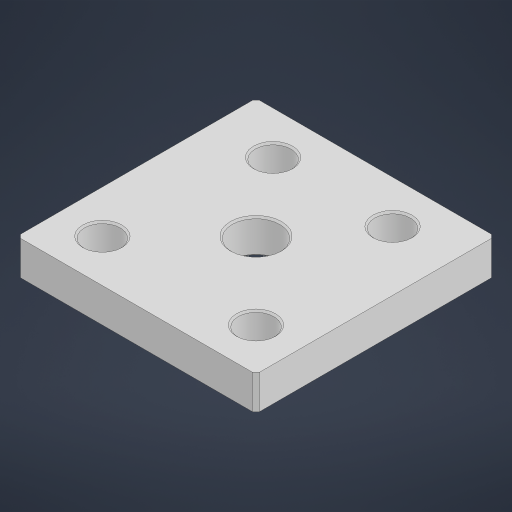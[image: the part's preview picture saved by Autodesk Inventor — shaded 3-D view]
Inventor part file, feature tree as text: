
AUTODESK INVENTOR PART (.ipt)
format: ipt  version: 2024.3 (Build 283343000, 343)  size: 202,752 bytes
history: native  units: mm
features: chamfer x2, sketch x1, extrude x1, hole x1
ambient origin geometry x8: Origin, YZ Plane, XZ Plane, XY Plane, X Axis, Y Axis, Z Axis, Center Point
bodies: Solid1 (feature_tree)
feature tree (5):
  sketch  "Sketch1"  dims[d0=70.0mm d1=45.0mm d2=35.0mm d3=14.0mm d4=10.0mm d5=0.0mm d6=10.5mm d7=20.0mm d8=4.0mm d9=2.0mm d10=90.0deg d11=8.0mm d12=20.594885mm d13=0.5mm d14=2.0mm d15=45.0deg d16=70.0mm d17=45.0mm d18=1.0mm d19=2.0mm d20=45.0deg]
  extrude  "Extrusion1"  Depth=70.0mm
  hole  "Hole1"  [1 undecoded]
  chamfer  "Chamfer1"  Distance=14.0mm
  chamfer  "Chamfer2"  Distance=10.0mm
note: 1 required parameter value undecoded (feature->parameter linkage not recoverable at this tier; creation-order binding heuristic only, values carry confidence <= 0.55)
